# Revit family: Basin_Prepackaged_System-Outdoor-Zoeller-18x30-912_Series
name_source: partatom
category: Mechanical Equipment
revit_build: Autodesk Revit 2014 (Build: 20130308_1515(x64)
units: mm (PartAtom-declared; Revit-internal decimal feet)

## types (16) — shared parameters
Assembly Code = D2030400
CW Connection = Yes
Cooling = Oil Filled
Cord Length = 180"
Default Elevation = 0"
Description = 912 Package Systems.
Diameter = 18"
Discharge Radius = 1"
Discharge Size = 2"
HW Connection = No
Height = 30"
Hertz = 60
Inlet Diameter = 4"
Inlet Radius = 2"
Manufacturer = Zoeller
Material = Foam-Zoeller-Poly Structural Foam (PSF)
Max. Operating Temp. = 130°F (54°C)
Motor Protection = Auto reset thermal overload
Operation = Automatic
Phase = 1
Price = Prices may vary. Please consult Manufacturer Representative for most up-to-date price list.
Product Documentation Link = http://cdn.qleapahead.com
Product Page URL = http://www.zoellerpumps.com
Pump Housing = Metal-Zoeller-Powder Coated Cast Iron
Radius = 9"
Solid Handling = 2" (50mm) spherical solids
URL = http://www.zoeller.com
Vent Connection = No
Voltage = 115 V
Waste Connection = Yes

## per-type parameters (varying)
| type | Alarm | Amps | Basin Type | Flow @ 5' | Insulation | Model | Nominal Radius | RPM | Shipping Weight | Type | Void Length |
| 912-0092/M266 - 115V, 10.4Amps, 128gpm@5' | No | 10.4 | Premium Polyethylene Structural Foam (PSF) w/ AFD | 128 GPM | Class A | 912-0092/M266 | 10 7/8" | 1750 | 73.00 lb | Split Phase | 15" |
| 912-0082/M264 - 115V, 9.4Amps, 90gpm@5' | No | 9.4 | Polythylene Structural Foam (PSF) | 90 GPM | Class B | 912-0082/M264 | 5" | 1725 | 61.00 lb | Permanent Split Capacitor | 15" |
| 912-1082/M264 - 115V, 9.4Amps, 90gpm@5' | Yes | 9.4 | Polythylene Structural Foam (PSF) with Alarm | 90 GPM | Class B | 912-1082/M264 | 5" | 1725 | 66.00 lb | Permanent Split Capacitor | -5" |
| 912-0090/M264 - 115V, 9.4Amps, 90gpm@5' | No | 9.4 | Premium Polyethylene Structural Foam (PSF) w/ AFD | 90 GPM | Class B | 912-0090/M264 | 10 7/8" | 1725 | 72.00 lb | Permanent Split Capacitor | 15" |
| 912-1090/M264 - 115V, 9.4Amps, 90gpm@5' | Yes | 9.4 | Premium Polyethylene Structural Foam (PSF) w/ AFD & Alarm | 90 GPM | Class B | 912-1090/M264 | 10 7/8" | 1725 | 72.00 lb | Permanent Split Capacitor | -5" |
| 912-0083/BN264 - 115V, 9.4Amps, 90gpm@5' | No | 9.4 | Polyethylene Structural Foam (PSF) | 90 GPM | Class B | 912-0083/BN264 | 5" | 1725 | 62.00 lb | Permanent Split Capacitor | 15" |
| 912-1083/BN264 - 115V, 9.4Amps, 90gpm@5' | Yes | 9.4 | Polythylene Structural Foam (PSF) with Alarm | 90 GPM | Class B | 912-1083/BN264 | 5" | 1725 | 67.00 lb | Permanent Split Capacitor | -5" |
| 912-0091/BN264 - 115V, 9.4Amps, 90gpm@5' | No | 9.4 | Premium Polyethylene Structural Foam (PSF) w/ AFD | 90 GPM | Class B | 912-0091/BN264 | 10 7/8" | 1725 | 72.00 lb | Permanent Split Capacitor | 15" |
| 912-1091/BN264 - 115V, 9.4Amps, 90gpm@5' | Yes | 9.4 | Premium Polyethylene Structural Foam (PSF) w/ AFD & Alarm | 90 GPM | Class B | 912-1091/BN264 | 10 7/8" | 1725 | 76.00 lb | Permanent Split Capacitor | -5" |
| 912-0084/M266 - 115V, 10.4Amps, 128gpm@5' | No | 10.4 | Polyethylene Structural Foam (PSF) | 128 GPM | Class A | 912-0084/M266 | 5" | 1750 | 62.00 lb | Split Phase | 15" |
| 912-1084/M266 - 115V, 10.4Amps, 128gpm@5' | Yes | 10.4 | Polyethylene Structural Foam (PSF) with Alarm | 128 GPM | Class A | 912-1084/M266 | 5" | 1750 | 67.00 lb | Split Phase | -5" |
| 912-1092/M266 - 115V, 10.4Amps, 128gpm@5' | Yes | 10.4 | Premium Polyethylene Structural Foam (PSF) w/ AFD & Alarm | 128 GPM | Class A | 912-1092/M266 | 10 7/8" | 1750 | 76.00 lb | Split Phase | -5" |
| 912-0085/BN266 - 115V, 10.4Amps, 128gpm@5' | No | 10.4 | Polyethylene Structural Foam (PSF) | 128 GPM | Class A | 912-0085/BN266 | 5" | 1750 | 63.00 lb | Split Phase | 15" |
| 912-1085/BN266 - 115V, 10.4Amps, 128gpm@5' | Yes | 10.4 | Polyethylene Structural Foam (PSF) with Alarm | 128 GPM | Class A | 912-1085/BN266 | 5" | 1750 | 68.00 lb | Split Phase | -5" |
| 912-0093/BN266 - 115V, 10.4Amps, 128gpm@5' | No | 10.4 | Premium Polyethylene Structural Foam (PSF) w/ AFD | 128 GPM | Class A | 912-0093/BN266 | 10 7/8" | 1750 | 73.00 lb | Split Phase | 15" |
| 912-1093/BN266 - 115V, 10.4Amps, 128gpm@5' | Yes | 10.4 | Premium Polyethylene Structural Foam (PSF) w/ AFD & Alarm | 128 GPM | Class A | 912-1093/BN266 | 10 7/8" | 1750 | 77.00 lb | Split Phase | -5" |

## geometry (parser evidence)
native form markers: Sweep x3
no freeform markers — native parametric forms only
